# Revit family: Poly Max - Ceiling Baffles
name_source: partatom
category: Specialty Equipment
units: mm (PartAtom-declared; Revit-internal decimal feet)

## family parameters
Always vertical = No
Cut with Voids When Loaded = No
Enable Cutting in Views = Yes
Maintain Annotation Orientation = No
OmniClass Number = 23.35.00.00
OmniClass Title = Covering, Cladding, and Finishes
Part Type = Normal
Room Calculation Point = No
Round Connector Dimension = Use Diameter
Shared = No
Work Plane-Based = Yes

## types (42) — shared parameters
Acoustics - NRC = Sound absorption varies from NRC 0.45 to 0.95 based on installation method used when tested per ASTM C423.
Assembly Code = C30
Default Elevation = 0' - 0"
Description = Acoustic Panels
Fire Rating = ASTM E84 - Class A
Manufacturer = Acoustical Surfaces, Inc.
Material = Poly Max
Model = Poly Max - Ceiling and Wall Panels
Recycled Content Percentage = 0%
Type Comments = Acoustic panels for vertical and horizontal surfaces
URL = https://www.acousticalsurfaces.com

## per-type parameters (varying)
| type | B | Finish | Length | T | Thickness Options | Width | ‍      0. Thickness 1/2" | ‍      1. Thickness 1" | ‍      2. Thickness 2" |
| 24 x 48 - 1 INCH - PRINTED GRAPHICS | 1' - 0" | Paint - Acoustical-Surfaces - Printed Graphics | 4' - 0" | 0' - 1" | 1 | 2' - 0" | No | Yes | No |
| 24 x 48 - 1 INCH - BLACK | 1' - 0" | Paint - Acoustical-Surfaces - Black | 4' - 0" | 0' - 1" | 1 | 2' - 0" | No | Yes | No |
| 24 x 48 - 1 INCH - BEIGE | 1' - 0" | Paint - Acoustical-Surfaces - Beige | 4' - 0" | 0' - 1" | 1 | 2' - 0" | No | Yes | No |
| 24 x 48 - 1 INCH - WHITE | 1' - 0" | Paint - Acoustical-Surfaces - White | 4' - 0" | 0' - 1" | 1 | 2' - 0" | No | Yes | No |
| 48 x 96 - 2 INCH - PRINTED GRAPHICS | 2' - 0" | Paint - Acoustical-Surfaces - Printed Graphics | 8' - 0" | 0' - 2" | 2 | 4' - 0" | No | No | Yes |
| 48 x 96 - 2 INCH - BLACK | 2' - 0" | Paint - Acoustical-Surfaces - Black | 8' - 0" | 0' - 2" | 2 | 4' - 0" | No | No | Yes |
| 48 x 96 - 2 INCH - BEIGE | 2' - 0" | Paint - Acoustical-Surfaces - Beige | 8' - 0" | 0' - 2" | 2 | 4' - 0" | No | No | Yes |
| 48 x 96 - 2 INCH - WHITE | 2' - 0" | Paint - Acoustical-Surfaces - White | 8' - 0" | 0' - 2" | 2 | 4' - 0" | No | No | Yes |
| 48 x 96 - 1 INCH - PRINTED GRAPHICS | 2' - 0" | Paint - Acoustical-Surfaces - Printed Graphics | 8' - 0" | 0' - 1" | 1 | 4' - 0" | No | Yes | No |
| 48 x 96 - 1 INCH - BLACK | 2' - 0" | Paint - Acoustical-Surfaces - Black | 8' - 0" | 0' - 1" | 1 | 4' - 0" | No | Yes | No |
| 48 x 96 - 1 INCH - BEIGE | 2' - 0" | Paint - Acoustical-Surfaces - Beige | 8' - 0" | 0' - 1" | 1 | 4' - 0" | No | Yes | No |
| 48 x 96 - 1 INCH - WHITE | 2' - 0" | Paint - Acoustical-Surfaces - White | 8' - 0" | 0' - 1" | 1 | 4' - 0" | No | Yes | No |
| 48 x 96 - HALF INCH - PRINTED GRAPHICS | 2' - 0" | Paint - Acoustical-Surfaces - Printed Graphics | 8' - 0" | 0' - 0 1/2" | 0 | 4' - 0" | Yes | No | No |
| 48 x 96 - HALF INCH - LIME | 2' - 0" | Paint - Acoustical-Surfaces - Lime | 8' - 0" | 0' - 0 1/2" | 0 | 4' - 0" | Yes | No | No |
| 48 x 96 - HALF INCH - ORANGE | 2' - 0" | Paint - Acoustical-Surfaces - Orange | 8' - 0" | 0' - 0 1/2" | 0 | 4' - 0" | Yes | No | No |
| 48 x 96 - HALF INCH - RED | 2' - 0" | Paint - Acoustical-Surfaces - Red | 8' - 0" | 0' - 0 1/2" | 0 | 4' - 0" | Yes | No | No |
| 48 x 96 - HALF INCH - PURPLE | 2' - 0" | Paint - Acoustical-Surfaces - Purple | 8' - 0" | 0' - 0 1/2" | 0 | 4' - 0" | Yes | No | No |
| 48 x 96 - HALF INCH - BLUE | 2' - 0" | Paint - Acoustical-Surfaces - Blue | 8' - 0" | 0' - 0 1/2" | 0 | 4' - 0" | Yes | No | No |
| 48 x 96 - HALF INCH - BLACK | 2' - 0" | Paint - Acoustical-Surfaces - Black | 8' - 0" | 0' - 0 1/2" | 0 | 4' - 0" | Yes | No | No |
| 48 x 96 - HALF INCH - GREY | 2' - 0" | Paint - Acoustical-Surfaces - Grey | 8' - 0" | 0' - 0 1/2" | 0 | 4' - 0" | Yes | No | No |
| 48 x 96 - HALF INCH - SILVER | 2' - 0" | Paint - Acoustical-Surfaces - Silver | 8' - 0" | 0' - 0 1/2" | 0 | 4' - 0" | Yes | No | No |
| 48 x 96 - HALF INCH - BROWN | 2' - 0" | Paint - Acoustical-Surfaces - Brown | 8' - 0" | 0' - 0 1/2" | 0 | 4' - 0" | Yes | No | No |
| 48 x 96 - HALF INCH - TAN | 2' - 0" | Paint - Acoustical-Surfaces - Tan | 8' - 0" | 0' - 0 1/2" | 0 | 4' - 0" | Yes | No | No |
| 48 x 96 - HALF INCH - WHITE | 2' - 0" | Paint - Acoustical-Surfaces - White | 8' - 0" | 0' - 0 1/2" | 0 | 4' - 0" | Yes | No | No |
| 48 x 96 - HALF INCH - BEIGE | 2' - 0" | Paint - Acoustical-Surfaces - Beige | 8' - 0" | 0' - 0 1/2" | 0 | 4' - 0" | Yes | No | No |
| 24 x 48 - 2 INCH - PRINTED GRAPHICS | 1' - 0" | Paint - Acoustical-Surfaces - Printed Graphics | 4' - 0" | 0' - 2" | 2 | 2' - 0" | No | No | Yes |
| 24 x 48 - 2 INCH - BLACK | 1' - 0" | Paint - Acoustical-Surfaces - Black | 4' - 0" | 0' - 2" | 2 | 2' - 0" | No | No | Yes |
| 24 x 48 - 2 INCH - BEIGE | 1' - 0" | Paint - Acoustical-Surfaces - Beige | 4' - 0" | 0' - 2" | 2 | 2' - 0" | No | No | Yes |
| 24 x 48 - 2 INCH - WHITE | 1' - 0" | Paint - Acoustical-Surfaces - White | 4' - 0" | 0' - 2" | 2 | 2' - 0" | No | No | Yes |
| 24 x 48 - HALF INCH - PRINTED GRAPHICS | 1' - 0" | Paint - Acoustical-Surfaces - Printed Graphics | 4' - 0" | 0' - 0 1/2" | 0 | 2' - 0" | Yes | No | No |
| 24 x 48 - HALF INCH - LIME | 1' - 0" | Paint - Acoustical-Surfaces - Lime | 4' - 0" | 0' - 0 1/2" | 0 | 2' - 0" | Yes | No | No |
| 24 x 48 - HALF INCH - ORANGE | 1' - 0" | Paint - Acoustical-Surfaces - Orange | 4' - 0" | 0' - 0 1/2" | 0 | 2' - 0" | Yes | No | No |
| 24 x 48 - HALF INCH - RED | 1' - 0" | Paint - Acoustical-Surfaces - Red | 4' - 0" | 0' - 0 1/2" | 0 | 2' - 0" | Yes | No | No |
| 24 x 48 - HALF INCH - PURPLE | 1' - 0" | Paint - Acoustical-Surfaces - Purple | 4' - 0" | 0' - 0 1/2" | 0 | 2' - 0" | Yes | No | No |
| 24 x 48 - HALF INCH - BLUE | 1' - 0" | Paint - Acoustical-Surfaces - Blue | 4' - 0" | 0' - 0 1/2" | 0 | 2' - 0" | Yes | No | No |
| 24 x 48 - HALF INCH - BLACK | 1' - 0" | Paint - Acoustical-Surfaces - Black | 4' - 0" | 0' - 0 1/2" | 0 | 2' - 0" | Yes | No | No |
| 24 x 48 - HALF INCH - GREY | 1' - 0" | Paint - Acoustical-Surfaces - Grey | 4' - 0" | 0' - 0 1/2" | 0 | 2' - 0" | Yes | No | No |
| 24 x 48 - HALF INCH - SILVER | 1' - 0" | Paint - Acoustical-Surfaces - Silver | 4' - 0" | 0' - 0 1/2" | 0 | 2' - 0" | Yes | No | No |
| 24 x 48 - HALF INCH - BROWN | 1' - 0" | Paint - Acoustical-Surfaces - Brown | 4' - 0" | 0' - 0 1/2" | 0 | 2' - 0" | Yes | No | No |
| 24 x 48 - HALF INCH - TAN | 1' - 0" | Paint - Acoustical-Surfaces - Tan | 4' - 0" | 0' - 0 1/2" | 0 | 2' - 0" | Yes | No | No |
| 24 x 48 - HALF INCH - BEIGE | 1' - 0" | Paint - Acoustical-Surfaces - Beige | 4' - 0" | 0' - 0 1/2" | 0 | 2' - 0" | Yes | No | No |
| 24 x 48 - HALF INCH - WHITE | 1' - 0" | Paint - Acoustical-Surfaces - White | 4' - 0" | 0' - 0 1/2" | 0 | 2' - 0" | Yes | No | No |

## geometry (parser evidence)
native form markers: Sweep x8
no freeform markers — native parametric forms only
